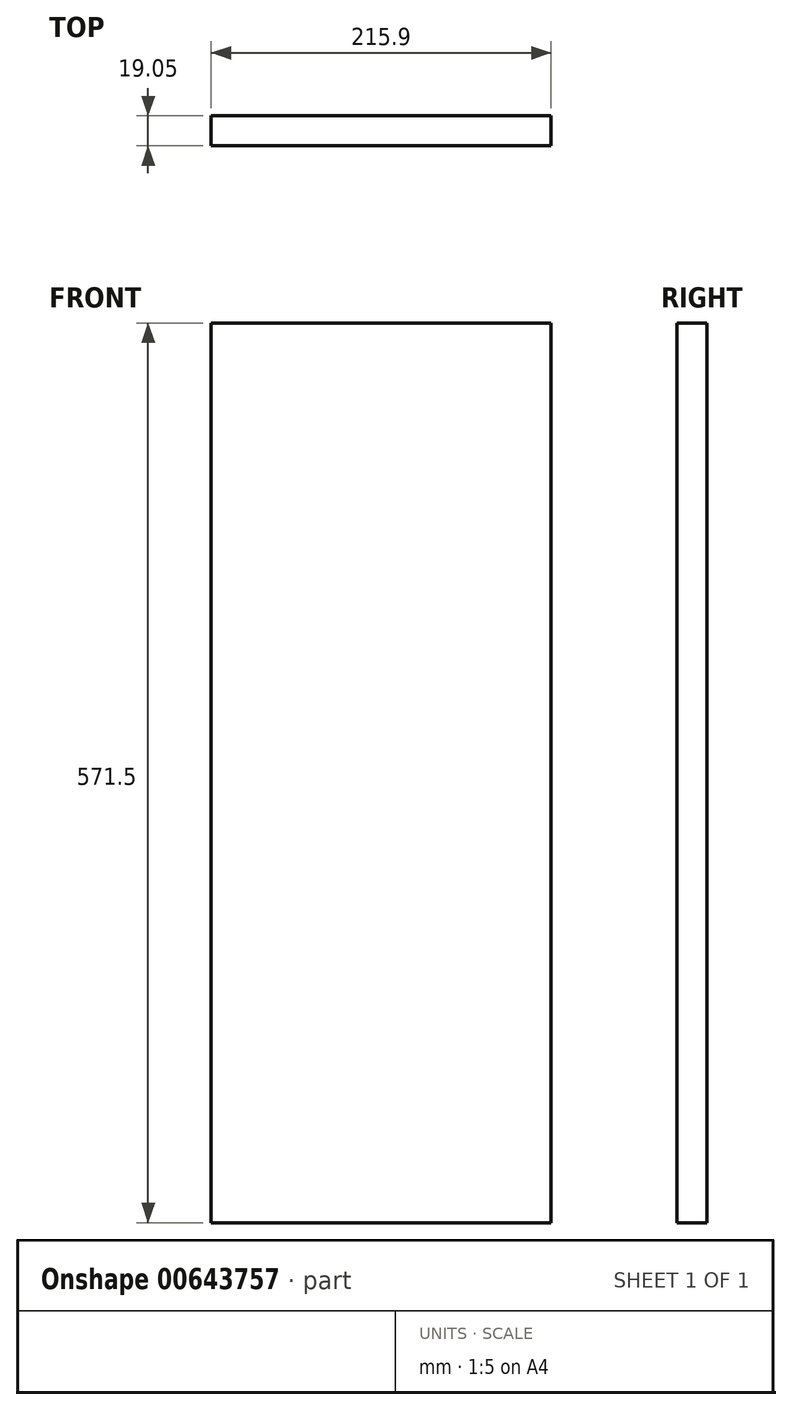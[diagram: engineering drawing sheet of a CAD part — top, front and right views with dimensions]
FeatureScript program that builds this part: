
annotation { "Feature Type Name" : "Feature", "Feature Type Description" : "" }
export const myFeature = defineFeature(function(context is Context, id is Id, definition is map)
    precondition{}
    {
        {
            var Q0;
            Q0=qCreatedBy(makeId("Front.planeOp"),FACE);
            var sketch = newSketch(context, id + "F0", { "sketchPlane" : qUnion([Q0])});
            skLineSegment(sketch, "E0.bottom", {"start": v(0, 0) * mm, "end": v(215.9, 0) * mm});
            skLineSegment(sketch, "E0.top", {"start": v(0, 571.5) * mm, "end": v(215.9, 571.5) * mm});
            skLineSegment(sketch, "E0.left", {"start": v(0, 0) * mm, "end": v(0, 571.5) * mm});
            skLineSegment(sketch, "E0.right", {"start": v(215.9, 0) * mm, "end": v(215.9, 571.5) * mm});
            skSolve(sketch);
        }
        {
            var Q0;
            Q0=makeQuery(id+"F0.imprint","IMPRINT",FACE,{"disambiguationData":[TD([[makeQuery(id+"F0.imprint","IMPRINT",EDGE,{"derivedFrom":sQuery(id+"F0.wireOp",EDGE,"E0.bottom")}),1.0]])]});
            extrude(context, id + "F1", {"entities" : qUnion([Q0]), "depth" : 19.05 * mm, "offsetDistance" : 25.4 * mm});
        }
    });
